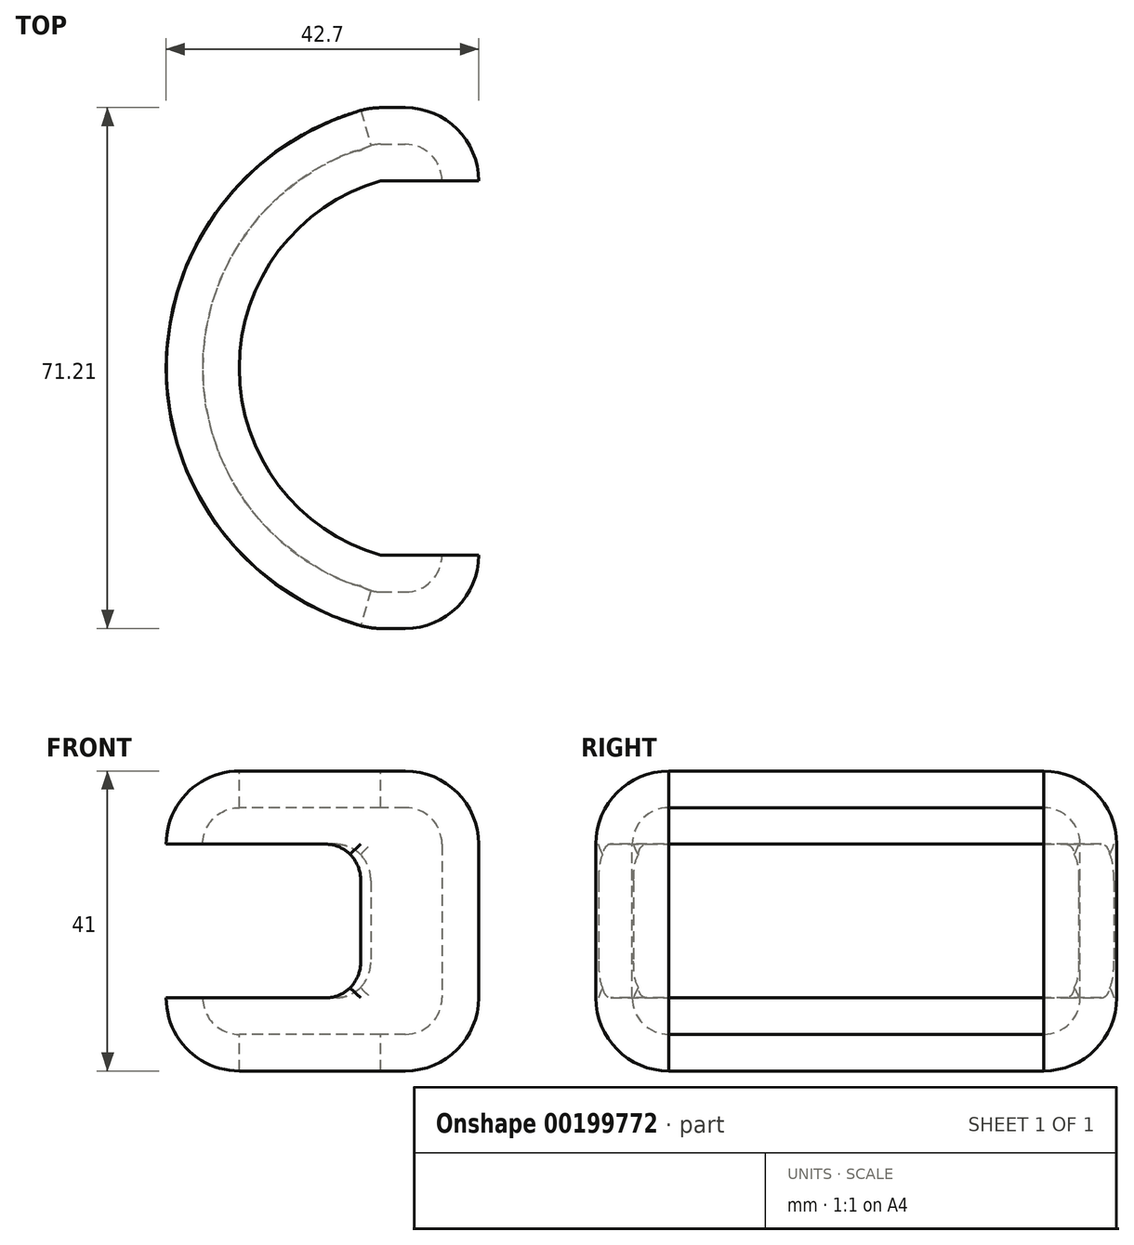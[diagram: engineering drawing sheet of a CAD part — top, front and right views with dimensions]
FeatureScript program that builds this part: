
annotation { "Feature Type Name" : "Feature", "Feature Type Description" : "" }
export const myFeature = defineFeature(function(context is Context, id is Id, definition is map)
    precondition{}
    {
        {
            var Q0;
            Q0=qCreatedBy(makeId("Top.planeOp"),FACE);
            var sketch = newSketch(context, id + "F0", { "sketchPlane" : qUnion([Q0])});
            skArc(sketch, "E0", {"start": v(0, 31.02) * mm, "mid": v(-28.06, -4.59) * mm, "end": v(0, -40.2) * mm});
            skLineSegment(sketch, "E1.bottom", {"start": v(0, -40.2) * mm, "end": v(14.64, -40.2) * mm});
            skLineSegment(sketch, "E1.top", {"start": v(0, 31.02) * mm, "end": v(14.64, 31.02) * mm});
            skLineSegment(sketch, "E1.right", {"start": v(14.64, -40.2) * mm, "end": v(14.64, 31.02) * mm});
            skSolve(sketch);
        }
        {
            var Q0;
            Q0 = qSketchRegion(id + "F0", true);
            extrude(context, id + "F1", {"entities" : qUnion([Q0]), "depth" : 41 * mm});
        }
        {
            var Q0;
            Q0=makeQuery(id+"F1.opExtrude","SWEPT_EDGE",EDGE,{"disambiguationData":[OSD([sQuery(id+"F0.wireOp",EDGE,"E0"),sQuery(id+"F0.wireOp",EDGE,"E1.bottom")])]});
            var Q1;
            Q1=makeQuery(id+"F1.opExtrude","SWEPT_EDGE",EDGE,{"disambiguationData":[OSD([sQuery(id+"F0.wireOp",EDGE,"E1.bottom"),sQuery(id+"F0.wireOp",EDGE,"E1.right")])]});
            var Q2;
            Q2=makeQuery(id+"F1.opExtrude","CAP_EDGE",EDGE,{"disambiguationData":[OSD([sQuery(id+"F0.wireOp",EDGE,"E1.right")])],"isStart":true});
            var Q3;
            Q3=makeQuery(id+"F1.opExtrude","CAP_EDGE",EDGE,{"disambiguationData":[OSD([sQuery(id+"F0.wireOp",EDGE,"E1.right")])],"isStart":false});
            var Q4;
            Q4=makeQuery(id+"F1.opExtrude","CAP_EDGE",EDGE,{"disambiguationData":[OSD([sQuery(id+"F0.wireOp",EDGE,"E0")])],"isStart":false});
            var Q5;
            Q5=makeQuery(id+"F1.opExtrude","CAP_EDGE",EDGE,{"disambiguationData":[OSD([sQuery(id+"F0.wireOp",EDGE,"E0")])],"isStart":true});
            var Q6;
            Q6=makeQuery(id+"F1.opExtrude","SWEPT_EDGE",EDGE,{"disambiguationData":[OSD([sQuery(id+"F0.wireOp",EDGE,"E0"),sQuery(id+"F0.wireOp",EDGE,"E1.top")])]});
            var Q7;
            Q7=makeQuery(id+"F1.opExtrude","SWEPT_EDGE",EDGE,{"disambiguationData":[OSD([sQuery(id+"F0.wireOp",EDGE,"E1.top"),sQuery(id+"F0.wireOp",EDGE,"E1.right")])]});
            var Q8;
            Q8=makeQuery(id+"F1.opExtrude","CAP_EDGE",EDGE,{"disambiguationData":[OSD([sQuery(id+"F0.wireOp",EDGE,"E1.bottom")])],"isStart":true});
            var Q9;
            Q9=makeQuery(id+"F1.opExtrude","CAP_EDGE",EDGE,{"disambiguationData":[OSD([sQuery(id+"F0.wireOp",EDGE,"E1.bottom")])],"isStart":false});
            var Q10;
            Q10=makeQuery(id+"F1.opExtrude","CAP_EDGE",EDGE,{"disambiguationData":[OSD([sQuery(id+"F0.wireOp",EDGE,"E1.top")])],"isStart":true});
            var Q11;
            Q11=makeQuery(id+"F1.opExtrude","CAP_EDGE",EDGE,{"disambiguationData":[OSD([sQuery(id+"F0.wireOp",EDGE,"E1.top")])],"isStart":false});
            fillet(context, id + "F2", {"entities" : qUnion([Q0, Q1, Q2, Q3, Q4, Q5, Q6, Q7, Q8, Q9, Q10, Q11]), "radius" : 10 * mm, "tangentPropagation" : true, "allowEdgeOverflow" : false});
        }
        {
            var Q0;
            Q0=makeQuery(id+"F1.opExtrude","CAP_FACE",FACE,{"disambiguationData":[OSD([sQuery(id+"F0.wireOp",EDGE,"E0"),sQuery(id+"F0.wireOp",EDGE,"E1.bottom"),sQuery(id+"F0.wireOp",EDGE,"E1.top"),sQuery(id+"F0.wireOp",EDGE,"E1.right")])],"isStart":false});
            var Q1;
            {var subQ0=sQuery(id+"F0.wireOp",EDGE,"E1.right");Q1=makeQuery(id+"F2.opFillet","BLEND_FACE",FACE,{"disambiguationData":[OSD([subQ0]),TDD([makeQuery(id+"F1.opExtrude","CAP_EDGE",EDGE,{"disambiguationData":[OSD([subQ0])],"isStart":false})])]});}
            var Q2;
            {var subQ0=sQuery(id+"F0.wireOp",EDGE,"E1.right");Q2=makeQuery(id+"F2.opFillet","BLEND_FACE",FACE,{"disambiguationData":[OSD([subQ0]),TDD([makeQuery(id+"F1.opExtrude","CAP_EDGE",EDGE,{"disambiguationData":[OSD([subQ0])],"isStart":true})])]});}
            var Q3;
            Q3=makeQuery(id+"F1.opExtrude","SWEPT_FACE",FACE,{"disambiguationData":[OSD([sQuery(id+"F0.wireOp",EDGE,"E1.right")])]});
            var Q4;
            Q4=makeQuery(id+"F1.opExtrude","CAP_FACE",FACE,{"disambiguationData":[OSD([sQuery(id+"F0.wireOp",EDGE,"E0"),sQuery(id+"F0.wireOp",EDGE,"E1.bottom"),sQuery(id+"F0.wireOp",EDGE,"E1.top"),sQuery(id+"F0.wireOp",EDGE,"E1.right")])],"isStart":true});
            var Q5;
            Q5=makeQuery(id+"F1.opExtrude","SWEPT_FACE",FACE,{"disambiguationData":[OSD([sQuery(id+"F0.wireOp",EDGE,"E0")])]});
            shell(context, id + "F3", {"entities" : qUnion([Q0, Q1, Q2, Q3, Q4, Q5]), "thickness" : 5 * mm});
        }
        {
            var Q0;
            {var subQ0=sQuery(id+"F0.wireOp",EDGE,"E0");var subQ1=sQuery(id+"F0.wireOp",EDGE,"E1.bottom");Q0=makeQuery(id+"F3.opShell","SHELL_CAP_EDGE",EDGE,{"derivedFrom":[makeQuery(id+"F2.opFillet","BLEND_VERTEX",VERTEX,{"blendedFrom":[makeQuery(id+"F1.opExtrude","CAP_VERTEX",VERTEX,{"disambiguationData":[OSD([subQ0,subQ1])],"isStart":false}),makeQuery(id+"F1.opExtrude","SWEPT_EDGE",EDGE,{"disambiguationData":[OSD([subQ0,subQ1])]}),makeQuery(id+"F1.opExtrude","CAP_EDGE",EDGE,{"disambiguationData":[OSD([subQ0])],"isStart":false}),makeQuery(id+"F1.opExtrude","SWEPT_FACE",FACE,{"disambiguationData":[OSD([subQ0])]})],"blendedInto":[makeQuery(id+"F1.opExtrude","SWEPT_FACE",FACE,{"disambiguationData":[OSD([subQ0])]})]})]});}
            var Q1;
            {var subQ0=sQuery(id+"F0.wireOp",EDGE,"E0");var subQ1=sQuery(id+"F0.wireOp",EDGE,"E1.bottom");Q1=makeQuery(id+"F3.opShell","SHELL_CAP_EDGE",EDGE,{"derivedFrom":[makeQuery(id+"F2.opFillet","BLEND_VERTEX",VERTEX,{"blendedFrom":[makeQuery(id+"F1.opExtrude","CAP_VERTEX",VERTEX,{"disambiguationData":[OSD([subQ0,subQ1])],"isStart":true}),makeQuery(id+"F1.opExtrude","SWEPT_EDGE",EDGE,{"disambiguationData":[OSD([subQ0,subQ1])]}),makeQuery(id+"F1.opExtrude","CAP_EDGE",EDGE,{"disambiguationData":[OSD([subQ0])],"isStart":true}),makeQuery(id+"F1.opExtrude","SWEPT_FACE",FACE,{"disambiguationData":[OSD([subQ0])]})],"blendedInto":[makeQuery(id+"F1.opExtrude","SWEPT_FACE",FACE,{"disambiguationData":[OSD([subQ0])]})]})]});}
            var Q2;
            {var subQ0=sQuery(id+"F0.wireOp",EDGE,"E0");var subQ1=sQuery(id+"F0.wireOp",EDGE,"E1.top");Q2=makeQuery(id+"F3.opShell","SHELL_CAP_EDGE",EDGE,{"derivedFrom":[makeQuery(id+"F2.opFillet","BLEND_VERTEX",VERTEX,{"blendedFrom":[makeQuery(id+"F1.opExtrude","CAP_VERTEX",VERTEX,{"disambiguationData":[OSD([subQ0,subQ1])],"isStart":true}),makeQuery(id+"F1.opExtrude","SWEPT_EDGE",EDGE,{"disambiguationData":[OSD([subQ0,subQ1])]}),makeQuery(id+"F1.opExtrude","CAP_EDGE",EDGE,{"disambiguationData":[OSD([subQ0])],"isStart":true}),makeQuery(id+"F1.opExtrude","SWEPT_FACE",FACE,{"disambiguationData":[OSD([subQ0])]})],"blendedInto":[makeQuery(id+"F1.opExtrude","SWEPT_FACE",FACE,{"disambiguationData":[OSD([subQ0])]})]})]});}
            var Q3;
            {var subQ0=sQuery(id+"F0.wireOp",EDGE,"E0");var subQ1=sQuery(id+"F0.wireOp",EDGE,"E1.top");Q3=makeQuery(id+"F3.opShell","SHELL_CAP_EDGE",EDGE,{"derivedFrom":[makeQuery(id+"F2.opFillet","BLEND_VERTEX",VERTEX,{"blendedFrom":[makeQuery(id+"F1.opExtrude","CAP_VERTEX",VERTEX,{"disambiguationData":[OSD([subQ0,subQ1])],"isStart":false}),makeQuery(id+"F1.opExtrude","SWEPT_EDGE",EDGE,{"disambiguationData":[OSD([subQ0,subQ1])]}),makeQuery(id+"F1.opExtrude","CAP_EDGE",EDGE,{"disambiguationData":[OSD([subQ0])],"isStart":false}),makeQuery(id+"F1.opExtrude","SWEPT_FACE",FACE,{"disambiguationData":[OSD([subQ0])]})],"blendedInto":[makeQuery(id+"F1.opExtrude","SWEPT_FACE",FACE,{"disambiguationData":[OSD([subQ0])]})]})]});}
            fillet(context, id + "F4", {"entities" : qUnion([Q0, Q1, Q2, Q3]), "radius" : 5 * mm, "tangentPropagation" : true, "allowEdgeOverflow" : false});
        }
    });
